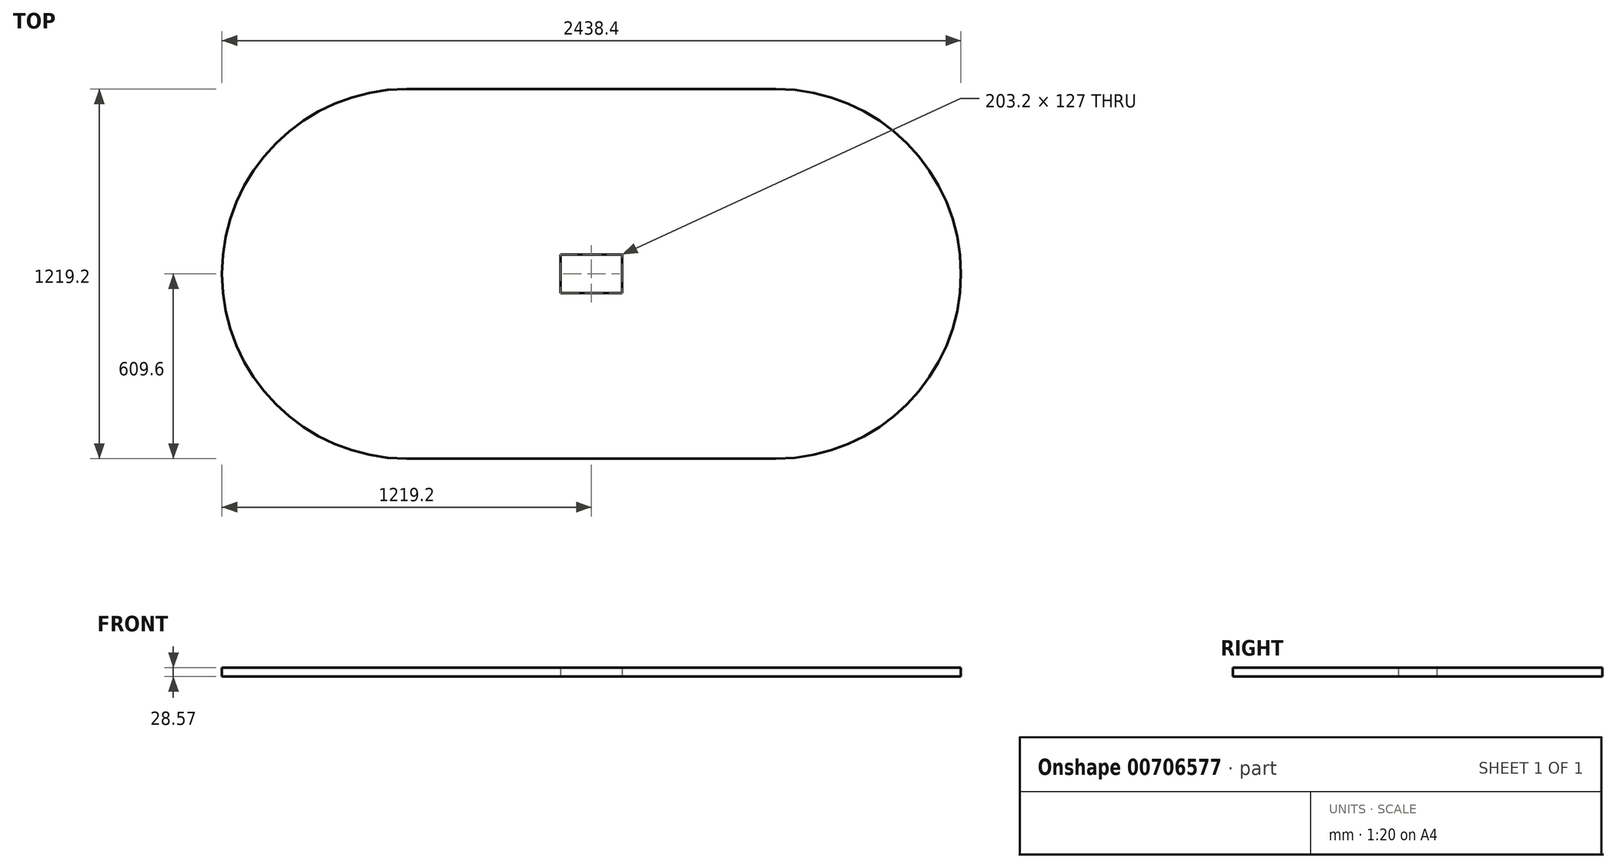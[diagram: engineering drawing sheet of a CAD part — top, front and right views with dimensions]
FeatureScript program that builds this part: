
annotation { "Feature Type Name" : "Feature", "Feature Type Description" : "" }
export const myFeature = defineFeature(function(context is Context, id is Id, definition is map)
    precondition{}
    {
        {
            var Q0;
            Q0=qCreatedBy(makeId("Top.planeOp"),FACE);
            var sketch = newSketch(context, id + "F0", { "sketchPlane" : qUnion([Q0])});
            skLineSegment(sketch, "E0.bottom", {"start": v(-1219.2, 609.6) * mm, "end": v(1219.2, 609.6) * mm});
            skLineSegment(sketch, "E0.top", {"start": v(-1219.2, -609.6) * mm, "end": v(1219.2, -609.6) * mm});
            skLineSegment(sketch, "E0.left", {"start": v(-1219.2, 609.6) * mm, "end": v(-1219.2, -609.6) * mm});
            skLineSegment(sketch, "E0.right", {"start": v(1219.2, 609.6) * mm, "end": v(1219.2, -609.6) * mm});
            skPoint(sketch, "E0.middle", {"position": v(0, 0) * mm});
            skLineSegment(sketch, "E1", {"start": v(-1219.2, 0) * mm, "end": v(-609.6, 0) * mm});
            skLineSegment(sketch, "E2", {"start": v(1219.2, 0) * mm, "end": v(609.6, 0) * mm});
            skArc(sketch, "E3", {"start": v(-609.6, 609.6) * mm, "mid": v(-1219.2, 0) * mm, "end": v(-609.6, -609.6) * mm});
            skArc(sketch, "E4", {"start": v(609.6, 609.6) * mm, "mid": v(1219.2, 0) * mm, "end": v(609.6, -609.6) * mm});
            skLineSegment(sketch, "E5.bottom", {"start": v(101.6, 63.5) * mm, "end": v(-101.6, 63.5) * mm});
            skLineSegment(sketch, "E5.top", {"start": v(101.6, -63.5) * mm, "end": v(-101.6, -63.5) * mm});
            skLineSegment(sketch, "E5.left", {"start": v(101.6, 63.5) * mm, "end": v(101.6, -63.5) * mm});
            skLineSegment(sketch, "E5.right", {"start": v(-101.6, 63.5) * mm, "end": v(-101.6, -63.5) * mm});
            skSolve(sketch);
        }
        {
            var Q0;
            Q0=makeQuery(id+"F0.imprint","IMPRINT",FACE,{"disambiguationData":[TD([[makeQuery(id+"F0.imprint","IMPRINT",EDGE,{"derivedFrom":sQuery(id+"F0.wireOp",EDGE,"E5.bottom")}),-1.0]])]});
            extrude(context, id + "F1", {"entities" : qUnion([Q0]), "depth" : 28.57 * mm, "offsetDistance" : 25.4 * mm});
        }
    });
